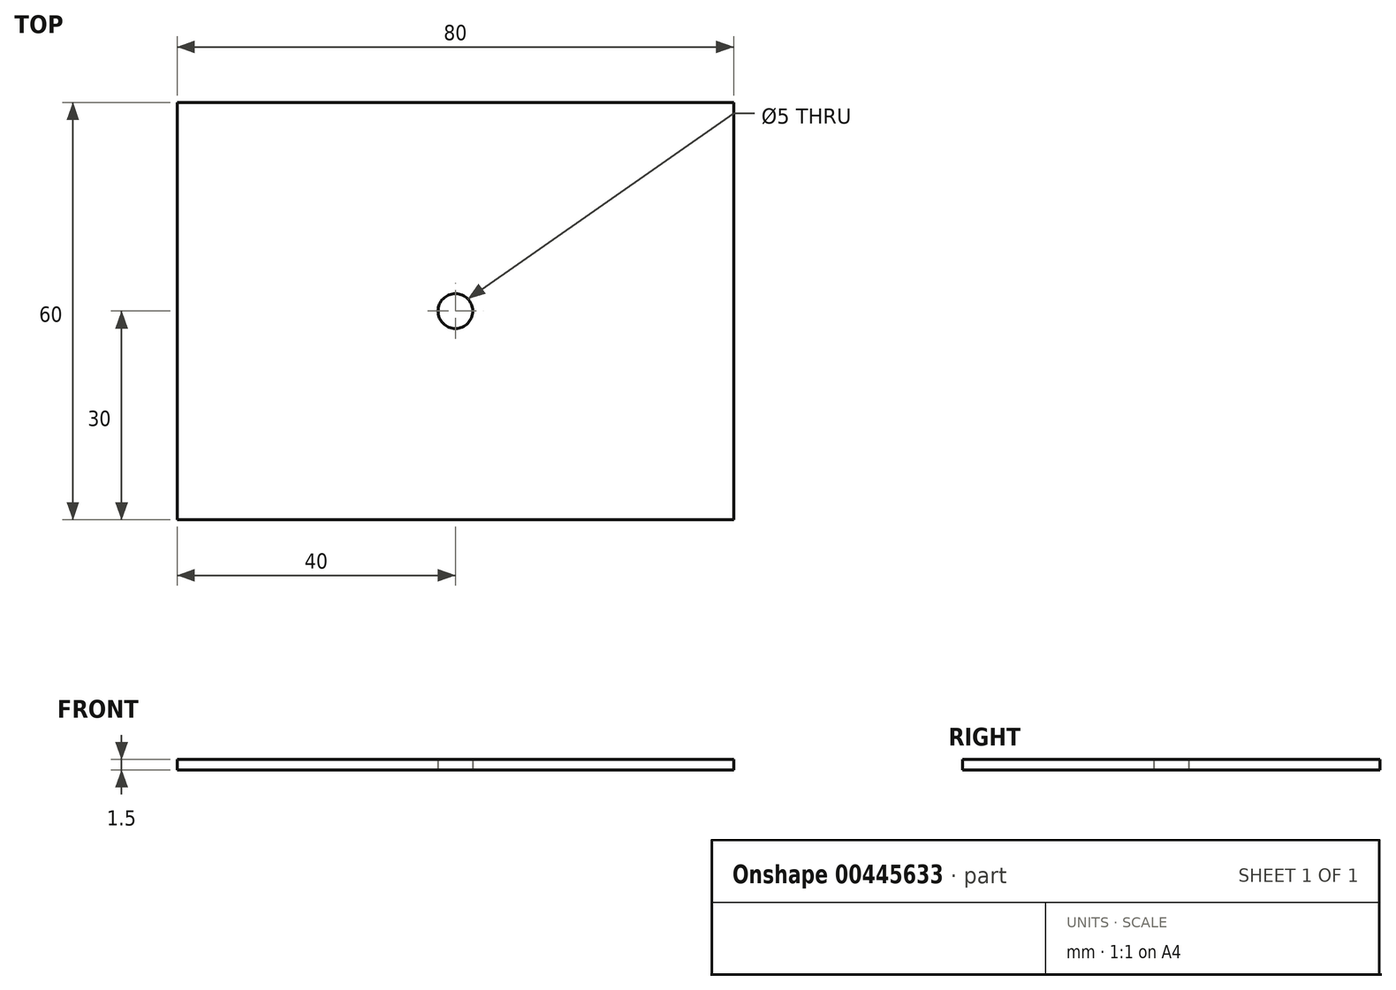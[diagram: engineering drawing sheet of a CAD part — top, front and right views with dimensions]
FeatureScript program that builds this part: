
annotation { "Feature Type Name" : "Feature", "Feature Type Description" : "" }
export const myFeature = defineFeature(function(context is Context, id is Id, definition is map)
    precondition{}
    {
        {
            var Q0;
            Q0=qCreatedBy(makeId("Top.planeOp"),FACE);
            var sketch = newSketch(context, id + "F0", { "sketchPlane" : qUnion([Q0])});
            skLineSegment(sketch, "E0.bottom", {"start": v(-40, 30) * mm, "end": v(40, 30) * mm});
            skLineSegment(sketch, "E0.top", {"start": v(-40, -30) * mm, "end": v(40, -30) * mm});
            skLineSegment(sketch, "E0.left", {"start": v(-40, 30) * mm, "end": v(-40, -30) * mm});
            skLineSegment(sketch, "E0.right", {"start": v(40, 30) * mm, "end": v(40, -30) * mm});
            skPoint(sketch, "E0.middle", {"position": v(0, 0) * mm});
            skCircle(sketch, "E1", {"center": v(0, 0) * mm, "radius": 2.5 * mm});
            skSolve(sketch);
        }
        {
            var Q0;
            Q0 = qSketchRegion(id + "F0", true);
            extrude(context, id + "F1", {"entities" : qUnion([Q0]), "depth" : 1.5 * mm});
        }
    });
